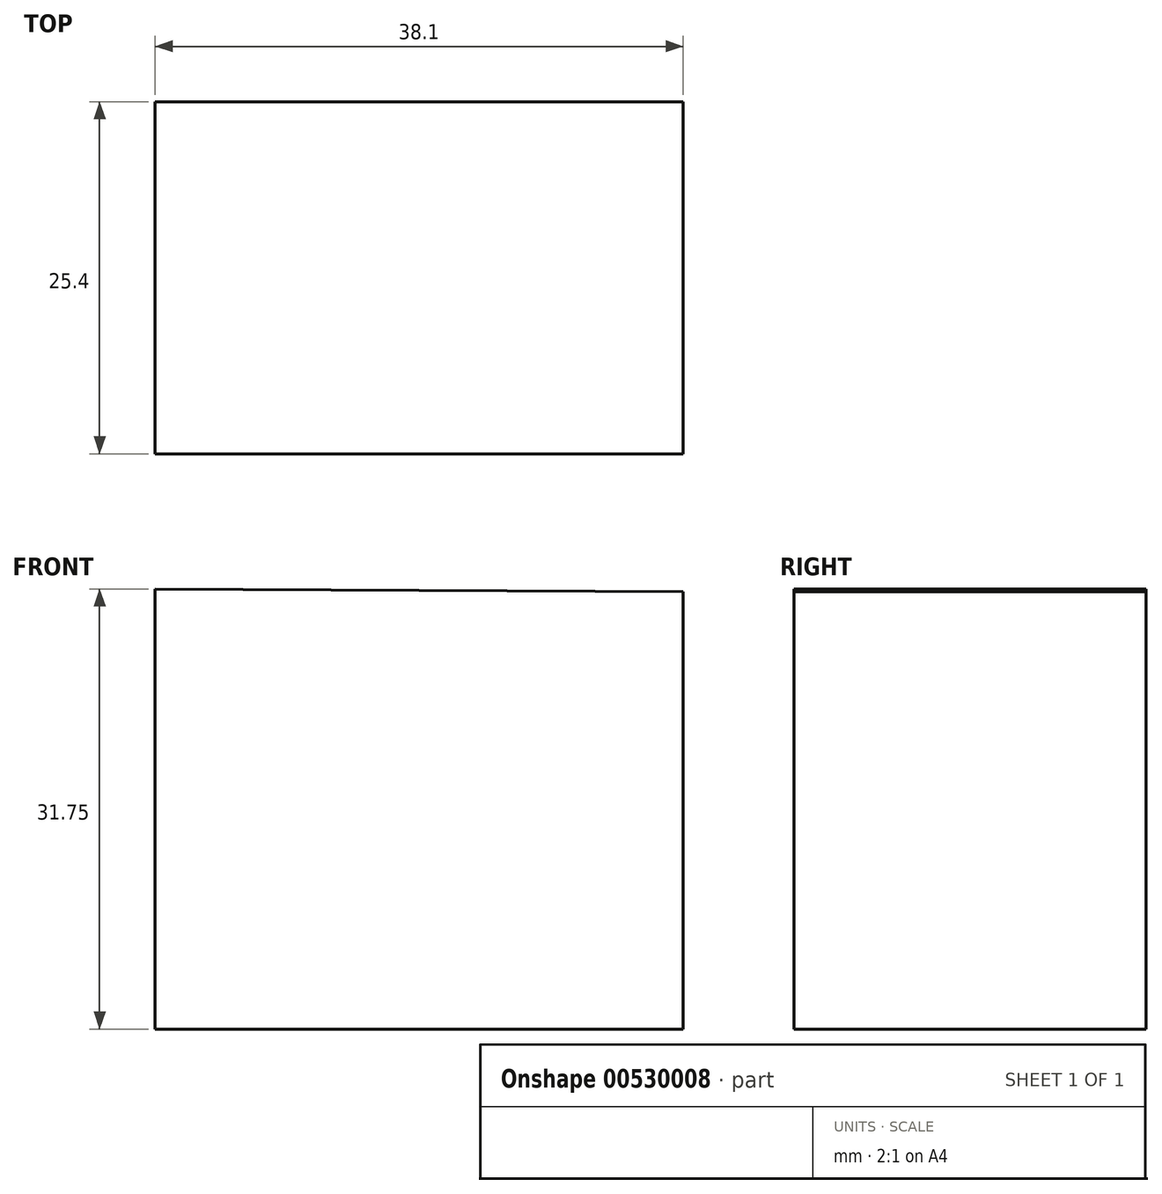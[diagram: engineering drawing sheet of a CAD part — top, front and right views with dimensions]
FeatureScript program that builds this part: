
annotation { "Feature Type Name" : "Feature", "Feature Type Description" : "" }
export const myFeature = defineFeature(function(context is Context, id is Id, definition is map)
    precondition{}
    {
        {
            var Q0;
            Q0=qCreatedBy(makeId("Front.planeOp"),FACE);
            var sketch = newSketch(context, id + "F0", { "sketchPlane" : qUnion([Q0])});
            skLineSegment(sketch, "E0", {"start": v(-58.47, 44.77) * mm, "end": v(-58.47, 13.02) * mm});
            skLineSegment(sketch, "E1", {"start": v(-58.47, 13.02) * mm, "end": v(-20.37, 13.02) * mm});
            skLineSegment(sketch, "E2", {"start": v(-20.37, 13.02) * mm, "end": v(-20.37, 44.56) * mm});
            skLineSegment(sketch, "E3", {"start": v(-58.47, 44.77) * mm, "end": v(-20.37, 44.56) * mm});
            skSolve(sketch);
        }
        {
            var Q0;
            Q0=makeQuery(id+"F0.imprint","IMPRINT",FACE,{"disambiguationData":[TD([[makeQuery(id+"F0.imprint","IMPRINT",EDGE,{"derivedFrom":sQuery(id+"F0.wireOp",EDGE,"E0")}),1.0]])]});
            extrude(context, id + "F1", {"entities" : qUnion([Q0]), "depth" : 25.4 * mm, "offsetDistance" : 25.4 * mm});
        }
    });
